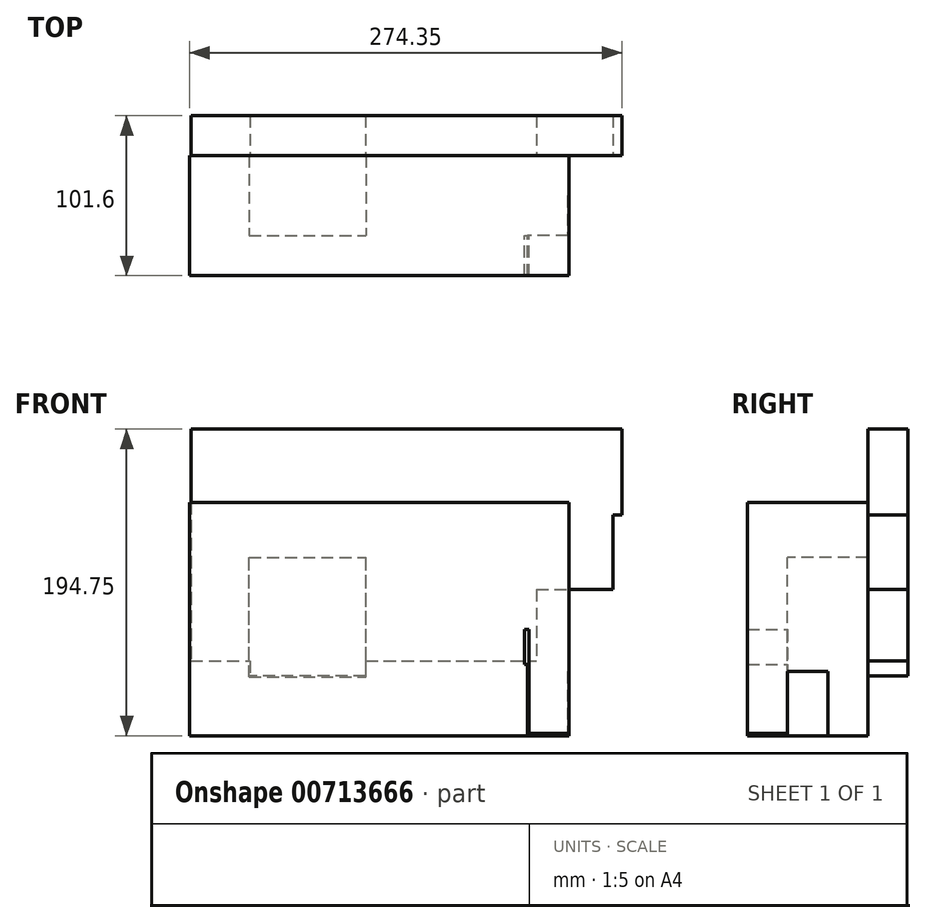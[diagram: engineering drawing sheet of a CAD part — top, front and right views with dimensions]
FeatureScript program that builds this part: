
annotation { "Feature Type Name" : "Feature", "Feature Type Description" : "" }
export const myFeature = defineFeature(function(context is Context, id is Id, definition is map)
    precondition{}
    {
        {
            var Q0;
            Q0=qCreatedBy(makeId("Front.planeOp"),FACE);
            var sketch = newSketch(context, id + "F0", { "sketchPlane" : qUnion([Q0])});
            skLineSegment(sketch, "E0.bottom", {"start": v(-136.7, -9.97) * mm, "end": v(75.91, -9.97) * mm});
            skLineSegment(sketch, "E0.top", {"start": v(-136.7, -32.2) * mm, "end": v(75.91, -32.2) * mm});
            skLineSegment(sketch, "E0.left", {"start": v(-136.7, -9.97) * mm, "end": v(-136.7, -32.2) * mm});
            skLineSegment(sketch, "E0.right", {"start": v(75.91, -9.97) * mm, "end": v(75.91, -32.2) * mm});
            skLineSegment(sketch, "E1.bottom", {"start": v(-136.7, -32.2) * mm, "end": v(77.82, -32.2) * mm});
            skLineSegment(sketch, "E1.top", {"start": v(-136.7, -77.37) * mm, "end": v(77.82, -77.37) * mm});
            skLineSegment(sketch, "E1.left", {"start": v(-136.7, -32.2) * mm, "end": v(-136.7, -77.37) * mm});
            skLineSegment(sketch, "E1.right", {"start": v(77.82, -32.2) * mm, "end": v(77.82, -77.37) * mm});
            skLineSegment(sketch, "E2.bottom", {"start": v(-136.7, -9.97) * mm, "end": v(78.83, -9.97) * mm});
            skLineSegment(sketch, "E2.top", {"start": v(-136.7, 70.86) * mm, "end": v(78.83, 70.86) * mm});
            skLineSegment(sketch, "E2.left", {"start": v(-136.7, -9.97) * mm, "end": v(-136.7, 70.86) * mm});
            skLineSegment(sketch, "E2.right", {"start": v(78.83, -9.97) * mm, "end": v(78.83, 70.86) * mm});
            skSolve(sketch);
        }
        {
            var Q0;
            Q0 = qSketchRegion(id + "F0", true);
            extrude(context, id + "F1", {"entities" : qUnion([Q0]), "depth" : 25.4 * mm, "offsetDistance" : 25.4 * mm});
        }
        {
            var Q0;
            Q0=makeQuery(id+"F1.opExtrude","SWEPT_FACE",FACE,{"disambiguationData":[OSD([sQuery(id+"F0.wireOp",EDGE,"E2.right")])]});
            var sketch = newSketch(context, id + "F2", { "sketchPlane" : qUnion([Q0])});
            skPoint(sketch, "E3.oppositeSnap0", {"position": v(-25.4, 30.45) * mm});
            skLineSegment(sketch, "E3.bottom", {"start": v(0, 70.86) * mm, "end": v(-25.4, 70.86) * mm});
            skLineSegment(sketch, "E3.top", {"start": v(0, -75.8) * mm, "end": v(-25.4, -75.8) * mm});
            skLineSegment(sketch, "E3.left", {"start": v(0, 70.86) * mm, "end": v(0, -75.8) * mm});
            skLineSegment(sketch, "E3.right", {"start": v(-25.4, 70.86) * mm, "end": v(-25.4, -75.8) * mm});
            skLineSegment(sketch, "E4.bottom", {"start": v(-13.69, 30.45) * mm, "end": v(0, 30.45) * mm});
            skLineSegment(sketch, "E4.top", {"start": v(-13.69, -9.97) * mm, "end": v(0, -9.97) * mm});
            skLineSegment(sketch, "E4.left", {"start": v(-13.69, 30.45) * mm, "end": v(-13.69, -9.97) * mm});
            skLineSegment(sketch, "E4.right", {"start": v(0, 30.45) * mm, "end": v(0, -9.97) * mm});
            skSolve(sketch);
        }
        {
            var Q0;
            Q0 = qSketchRegion(id + "F2", true);
            extrude(context, id + "F3", {"entities" : qUnion([Q0]), "operationType" : NewBodyOperationType.ADD, "depth" : 25.4 * mm, "offsetDistance" : 25.4 * mm});
        }
        {
            var Q0;
            Q0=makeQuery(id+"F3.boolean.opBoolean","MERGE",FACE,{"derivedFrom":[makeQuery(id+"F1.opExtrude","CAP_FACE",FACE,{"disambiguationData":[OSD([sQuery(id+"F0.wireOp",EDGE,"E0.left"),sQuery(id+"F0.wireOp",EDGE,"E0.right"),sQuery(id+"F0.wireOp",EDGE,"E1.bottom"),sQuery(id+"F0.wireOp",EDGE,"E1.top"),sQuery(id+"F0.wireOp",EDGE,"E1.left"),sQuery(id+"F0.wireOp",EDGE,"E1.right"),sQuery(id+"F0.wireOp",EDGE,"E2.bottom"),sQuery(id+"F0.wireOp",EDGE,"E2.top"),sQuery(id+"F0.wireOp",EDGE,"E2.left"),sQuery(id+"F0.wireOp",EDGE,"E2.right")])],"isStart":true}),makeQuery(id+"F3.opExtrude","SWEPT_FACE",FACE,{"disambiguationData":[OSD([sQuery(id+"F2.wireOp",EDGE,"E3.left"),sQuery(id+"F2.wireOp",EDGE,"E4.right")])]})]});
            var sketch = newSketch(context, id + "F4", { "sketchPlane" : qUnion([Q0])});
            skLineSegment(sketch, "E5.bottom", {"start": v(75.8, -77.37) * mm, "end": v(136.7, -77.37) * mm});
            skLineSegment(sketch, "E5.top", {"start": v(75.8, 70.86) * mm, "end": v(136.7, 70.86) * mm});
            skLineSegment(sketch, "E5.left", {"start": v(75.8, -77.37) * mm, "end": v(75.8, 70.86) * mm});
            skLineSegment(sketch, "E5.right", {"start": v(136.7, -77.37) * mm, "end": v(136.7, 70.86) * mm});
            skLineSegment(sketch, "E6.bottom", {"start": v(75.8, 70.86) * mm, "end": v(-17.93, 70.86) * mm});
            skLineSegment(sketch, "E6.top", {"start": v(75.8, -77.37) * mm, "end": v(-17.93, -77.37) * mm});
            skLineSegment(sketch, "E6.left", {"start": v(75.8, 70.86) * mm, "end": v(75.8, -77.37) * mm});
            skLineSegment(sketch, "E6.right", {"start": v(-17.93, 70.86) * mm, "end": v(-17.93, -77.37) * mm});
            skLineSegment(sketch, "E7.bottom", {"start": v(-17.93, -77.37) * mm, "end": v(-17.93, -77.37) * mm});
            skLineSegment(sketch, "E7.top", {"start": v(-17.93, 70.86) * mm, "end": v(-17.93, 70.86) * mm});
            skLineSegment(sketch, "E7.left", {"start": v(-17.93, -77.37) * mm, "end": v(-17.93, 70.86) * mm});
            skLineSegment(sketch, "E7.right", {"start": v(-17.93, -77.37) * mm, "end": v(-17.93, 70.86) * mm});
            skLineSegment(sketch, "E8.bottom", {"start": v(99.08, -40.05) * mm, "end": v(24.74, -40.05) * mm});
            skLineSegment(sketch, "E8.top", {"start": v(99.08, 35.82) * mm, "end": v(24.74, 35.82) * mm});
            skLineSegment(sketch, "E8.left", {"start": v(99.08, -40.05) * mm, "end": v(99.08, 35.82) * mm});
            skLineSegment(sketch, "E8.right", {"start": v(24.74, -40.05) * mm, "end": v(24.74, 35.82) * mm});
            skSolve(sketch);
        }
        {
            var Q0;
            Q0 = qSketchRegion(id + "F4", true);
            extrude(context, id + "F5", {"entities" : qUnion([Q0]), "operationType" : NewBodyOperationType.ADD, "depth" : 25.4 * mm, "offsetDistance" : 25.4 * mm});
        }
        {
            var Q0;
            Q0=makeQuery(id+"F5.opExtrude","CAP_FACE",FACE,{"disambiguationData":[OSD([sQuery(id+"F4.wireOp",EDGE,"E5.bottom"),sQuery(id+"F4.wireOp",EDGE,"E5.top"),sQuery(id+"F4.wireOp",EDGE,"E5.right"),sQuery(id+"F4.wireOp",EDGE,"E6.bottom"),sQuery(id+"F4.wireOp",EDGE,"E6.top"),sQuery(id+"F4.wireOp",EDGE,"E7.right"),sQuery(id+"F4.wireOp",EDGE,"E8.bottom"),sQuery(id+"F4.wireOp",EDGE,"E8.top"),sQuery(id+"F4.wireOp",EDGE,"E8.left"),sQuery(id+"F4.wireOp",EDGE,"E8.right")])],"isStart":false});
            var sketch = newSketch(context, id + "F6", { "sketchPlane" : qUnion([Q0])});
            skLineSegment(sketch, "E9.bottom", {"start": v(77.95, 14.77) * mm, "end": v(-17.93, 14.77) * mm});
            skLineSegment(sketch, "E9.top", {"start": v(77.95, 70.86) * mm, "end": v(-17.93, 70.86) * mm});
            skLineSegment(sketch, "E9.left", {"start": v(77.95, 14.77) * mm, "end": v(77.95, 70.86) * mm});
            skLineSegment(sketch, "E9.right", {"start": v(-17.93, 14.77) * mm, "end": v(-17.93, 70.86) * mm});
            skLineSegment(sketch, "E10.bottom", {"start": v(77.95, 70.86) * mm, "end": v(136.7, 70.86) * mm});
            skLineSegment(sketch, "E10.top", {"start": v(77.95, -77.37) * mm, "end": v(136.7, -77.37) * mm});
            skLineSegment(sketch, "E10.left", {"start": v(77.95, 70.86) * mm, "end": v(77.95, -77.37) * mm});
            skLineSegment(sketch, "E10.right", {"start": v(136.7, 70.86) * mm, "end": v(136.7, -77.37) * mm});
            skLineSegment(sketch, "E11.bottom", {"start": v(77.95, -77.37) * mm, "end": v(-17.93, -77.37) * mm});
            skLineSegment(sketch, "E11.left", {"start": v(77.95, -77.37) * mm, "end": v(77.95, 14.77) * mm});
            skLineSegment(sketch, "E11.right", {"start": v(-17.93, -77.37) * mm, "end": v(-17.93, 14.77) * mm});
            skLineSegment(sketch, "E12.bottom", {"start": v(24.74, 35.82) * mm, "end": v(99.08, 35.82) * mm});
            skLineSegment(sketch, "E12.top", {"start": v(24.74, -40.05) * mm, "end": v(99.08, -40.05) * mm});
            skLineSegment(sketch, "E12.left", {"start": v(24.74, 35.82) * mm, "end": v(24.74, -40.05) * mm});
            skLineSegment(sketch, "E12.right", {"start": v(99.08, 35.82) * mm, "end": v(99.08, -40.05) * mm});
            skSolve(sketch);
        }
        {
            var Q0;
            Q0 = qSketchRegion(id + "F6", true);
            extrude(context, id + "F7", {"entities" : qUnion([Q0]), "operationType" : NewBodyOperationType.ADD, "depth" : 25.4 * mm, "offsetDistance" : 25.4 * mm});
        }
        {
            var Q0;
            {var subQ0=sQuery(id+"F2.wireOp",EDGE,"E4.right");var subQ2=sQuery(id+"F2.wireOp",EDGE,"E3.left");var subQ5=sQuery(id+"F0.wireOp",EDGE,"E1.top");var subQ6=sQuery(id+"F0.wireOp",EDGE,"E1.bottom");var subQ7=sQuery(id+"F0.wireOp",EDGE,"E2.top");var subQ8=sQuery(id+"F0.wireOp",EDGE,"E2.bottom");var subQ9=sQuery(id+"F0.wireOp",EDGE,"E1.right");var subQ10=sQuery(id+"F0.wireOp",EDGE,"E0.right");Q0=makeQuery(id+"F5.boolean.opBoolean","SPLIT",FACE,{"disambiguationData":[TD([makeQuery(id+"F1.opExtrude","SWEPT_FACE",FACE,{"disambiguationData":[OSD([subQ10])]})])],"derivedFrom":makeQuery(id+"F3.boolean.opBoolean","MERGE",FACE,{"derivedFrom":[makeQuery(id+"F1.opExtrude","CAP_FACE",FACE,{"disambiguationData":[OSD([sQuery(id+"F0.wireOp",EDGE,"E0.left"),subQ10,subQ6,subQ5,sQuery(id+"F0.wireOp",EDGE,"E1.left"),subQ9,subQ8,subQ7,sQuery(id+"F0.wireOp",EDGE,"E2.left"),sQuery(id+"F0.wireOp",EDGE,"E2.right")])],"isStart":true}),makeQuery(id+"F3.opExtrude","SWEPT_FACE",FACE,{"disambiguationData":[OSD([subQ2,subQ0])]})]})});}
            var sketch = newSketch(context, id + "F8", { "sketchPlane" : qUnion([Q0])});
            skLineSegment(sketch, "E13.bottom", {"start": v(-104.23, 70.86) * mm, "end": v(-17.93, 70.86) * mm});
            skLineSegment(sketch, "E13.top", {"start": v(-104.23, -36.6) * mm, "end": v(-17.93, -36.6) * mm});
            skLineSegment(sketch, "E13.left", {"start": v(-104.23, 70.86) * mm, "end": v(-104.23, -36.6) * mm});
            skLineSegment(sketch, "E13.right", {"start": v(-17.93, 70.86) * mm, "end": v(-17.93, -36.6) * mm});
            skSolve(sketch);
        }
        {
            var Q0;
            Q0 = qSketchRegion(id + "F8", true);
            extrude(context, id + "F9", {"entities" : qUnion([Q0]), "operationType" : NewBodyOperationType.ADD, "depth" : 25.4 * mm, "offsetDistance" : 25.4 * mm});
        }
        {
            var Q0;
            {var subQ3=sQuery(id+"F0.wireOp",EDGE,"E1.right");var subQ5=sQuery(id+"F0.wireOp",EDGE,"E1.top");var subQ6=makeQuery(id+"F1.opExtrude","SWEPT_FACE",FACE,{"disambiguationData":[OSD([subQ5])]});var subQ7=sQuery(id+"F2.wireOp",EDGE,"E4.right");var subQ9=sQuery(id+"F2.wireOp",EDGE,"E3.left");var subQ12=sQuery(id+"F0.wireOp",EDGE,"E1.bottom");var subQ13=sQuery(id+"F0.wireOp",EDGE,"E2.top");var subQ14=sQuery(id+"F0.wireOp",EDGE,"E2.bottom");var subQ15=sQuery(id+"F0.wireOp",EDGE,"E0.right");Q0=makeQuery(id+"F9.boolean.opBoolean","SPLIT",FACE,{"disambiguationData":[TD([subQ6])],"derivedFrom":makeQuery(id+"F5.boolean.opBoolean","SPLIT",FACE,{"disambiguationData":[TD([makeQuery(id+"F1.opExtrude","SWEPT_FACE",FACE,{"disambiguationData":[OSD([subQ15])]})])],"derivedFrom":makeQuery(id+"F3.boolean.opBoolean","MERGE",FACE,{"derivedFrom":[makeQuery(id+"F1.opExtrude","CAP_FACE",FACE,{"disambiguationData":[OSD([sQuery(id+"F0.wireOp",EDGE,"E0.left"),subQ15,subQ12,subQ5,sQuery(id+"F0.wireOp",EDGE,"E1.left"),subQ3,subQ14,subQ13,sQuery(id+"F0.wireOp",EDGE,"E2.left"),sQuery(id+"F0.wireOp",EDGE,"E2.right")])],"isStart":true}),makeQuery(id+"F3.opExtrude","SWEPT_FACE",FACE,{"disambiguationData":[OSD([subQ9,subQ7])]})]})})});}
            var sketch = newSketch(context, id + "F10", { "sketchPlane" : qUnion([Q0])});
            skLineSegment(sketch, "E14.bottom", {"start": v(-103.22, -36.6) * mm, "end": v(-17.93, -36.6) * mm});
            skLineSegment(sketch, "E14.top", {"start": v(-103.22, -77.37) * mm, "end": v(-17.93, -77.37) * mm});
            skLineSegment(sketch, "E14.left", {"start": v(-103.22, -36.6) * mm, "end": v(-103.22, -77.37) * mm});
            skLineSegment(sketch, "E14.right", {"start": v(-17.93, -36.6) * mm, "end": v(-17.93, -77.37) * mm});
            skSolve(sketch);
        }
        {
            var Q0;
            Q0 = qSketchRegion(id + "F10", true);
            extrude(context, id + "F11", {"entities" : qUnion([Q0]), "operationType" : NewBodyOperationType.ADD, "depth" : 25.4 * mm, "offsetDistance" : 25.4 * mm});
        }
        {
            var Q0;
            Q0=makeQuery(id+"F11.boolean.opBoolean","MERGE",FACE,{"derivedFrom":[makeQuery(id+"F9.opExtrude","CAP_FACE",FACE,{"disambiguationData":[OSD([sQuery(id+"F8.wireOp",EDGE,"E13.bottom"),sQuery(id+"F8.wireOp",EDGE,"E13.top"),sQuery(id+"F8.wireOp",EDGE,"E13.left"),sQuery(id+"F8.wireOp",EDGE,"E13.right")])],"isStart":false}),makeQuery(id+"F11.opExtrude","CAP_FACE",FACE,{"disambiguationData":[OSD([sQuery(id+"F10.wireOp",EDGE,"E14.bottom"),sQuery(id+"F10.wireOp",EDGE,"E14.top"),sQuery(id+"F10.wireOp",EDGE,"E14.left"),sQuery(id+"F10.wireOp",EDGE,"E14.right")])],"isStart":false})]});
            var sketch = newSketch(context, id + "F12", { "sketchPlane" : qUnion([Q0])});
            skLineSegment(sketch, "E15.bottom", {"start": v(-104.23, 70.86) * mm, "end": v(-17.93, 70.86) * mm});
            skLineSegment(sketch, "E15.top", {"start": v(-104.23, -77.37) * mm, "end": v(-17.93, -77.37) * mm});
            skLineSegment(sketch, "E15.left", {"start": v(-104.23, 70.86) * mm, "end": v(-104.23, -77.37) * mm});
            skLineSegment(sketch, "E15.right", {"start": v(-17.93, 70.86) * mm, "end": v(-17.93, -77.37) * mm});
            skSolve(sketch);
        }
        {
            var Q0;
            Q0 = qSketchRegion(id + "F12", true);
            extrude(context, id + "F13", {"entities" : qUnion([Q0]), "operationType" : NewBodyOperationType.ADD, "depth" : 25.4 * mm, "offsetDistance" : 25.4 * mm});
        }
        {
            var Q0;
            Q0=makeQuery(id+"F13.boolean.opBoolean","MERGE",FACE,{"derivedFrom":[makeQuery(id+"F7.opExtrude","CAP_FACE",FACE,{"disambiguationData":[OSD([sQuery(id+"F6.wireOp",EDGE,"E9.top"),sQuery(id+"F6.wireOp",EDGE,"E9.right"),sQuery(id+"F6.wireOp",EDGE,"E10.bottom"),sQuery(id+"F6.wireOp",EDGE,"E10.top"),sQuery(id+"F6.wireOp",EDGE,"E10.right"),sQuery(id+"F6.wireOp",EDGE,"E11.bottom"),sQuery(id+"F6.wireOp",EDGE,"E11.right"),sQuery(id+"F6.wireOp",EDGE,"E12.bottom"),sQuery(id+"F6.wireOp",EDGE,"E12.top"),sQuery(id+"F6.wireOp",EDGE,"E12.left"),sQuery(id+"F6.wireOp",EDGE,"E12.right")])],"isStart":false}),makeQuery(id+"F13.opExtrude","CAP_FACE",FACE,{"disambiguationData":[OSD([sQuery(id+"F12.wireOp",EDGE,"E15.bottom"),sQuery(id+"F12.wireOp",EDGE,"E15.top"),sQuery(id+"F12.wireOp",EDGE,"E15.left"),sQuery(id+"F12.wireOp",EDGE,"E15.right")])],"isStart":false})]});
            var sketch = newSketch(context, id + "F14", { "sketchPlane" : qUnion([Q0])});
            skLineSegment(sketch, "E16.bottom", {"start": v(-104.23, 70.86) * mm, "end": v(70.52, 70.86) * mm});
            skLineSegment(sketch, "E16.top", {"start": v(-104.23, -77.37) * mm, "end": v(70.52, -77.37) * mm});
            skLineSegment(sketch, "E16.left", {"start": v(-104.23, 70.86) * mm, "end": v(-104.23, -77.37) * mm});
            skLineSegment(sketch, "E16.right", {"start": v(70.52, 70.86) * mm, "end": v(70.52, -77.37) * mm});
            skLineSegment(sketch, "E17.bottom", {"start": v(24.74, 35.82) * mm, "end": v(89.08, 35.82) * mm});
            skLineSegment(sketch, "E17.top", {"start": v(24.74, -26.86) * mm, "end": v(89.08, -26.86) * mm});
            skLineSegment(sketch, "E17.left", {"start": v(24.74, 35.82) * mm, "end": v(24.74, -26.86) * mm});
            skLineSegment(sketch, "E17.right", {"start": v(89.08, 35.82) * mm, "end": v(89.08, -26.86) * mm});
            skSolve(sketch);
        }
        {
            var Q0;
            {var subQ1=sQuery(id+"F14.wireOp",EDGE,"E16.bottom");Q0=makeQuery(id+"F14.imprint","IMPRINT",FACE,{"disambiguationData":[TD([[makeQuery(id+"F14.imprint","IMPRINT",EDGE,{"derivedFrom":subQ1}),1.0]])]});}
            var sketch = newSketch(context, id + "F15", { "sketchPlane" : qUnion([Q0])});
            skLineSegment(sketch, "E18.bottom", {"start": v(25.08, 34.42) * mm, "end": v(98.34, 34.42) * mm});
            skLineSegment(sketch, "E18.top", {"start": v(25.08, -39.32) * mm, "end": v(98.34, -39.32) * mm});
            skLineSegment(sketch, "E18.left", {"start": v(25.08, 34.42) * mm, "end": v(25.08, -39.32) * mm});
            skLineSegment(sketch, "E18.right", {"start": v(98.34, 34.42) * mm, "end": v(98.34, -39.32) * mm});
            skLineSegment(sketch, "E19.bottom", {"start": v(135.92, 117.38) * mm, "end": v(-83.47, 117.38) * mm});
            skLineSegment(sketch, "E19.top", {"start": v(135.92, -29.88) * mm, "end": v(-83.47, -29.88) * mm});
            skLineSegment(sketch, "E19.left", {"start": v(135.92, 117.38) * mm, "end": v(135.92, -29.88) * mm});
            skLineSegment(sketch, "E19.right", {"start": v(-83.47, 117.38) * mm, "end": v(-83.47, -29.88) * mm});
            skLineSegment(sketch, "E20.bottom", {"start": v(-83.47, 62.9) * mm, "end": v(-132.05, 62.9) * mm});
            skLineSegment(sketch, "E20.top", {"start": v(-83.47, 15.43) * mm, "end": v(-132.05, 15.43) * mm});
            skLineSegment(sketch, "E20.left", {"start": v(-83.47, 62.9) * mm, "end": v(-83.47, 15.43) * mm});
            skLineSegment(sketch, "E20.right", {"start": v(-132.05, 62.9) * mm, "end": v(-132.05, 15.43) * mm});
            skLineSegment(sketch, "E21.left", {"start": v(-83.47, 62.9) * mm, "end": v(-83.47, 62.9) * mm});
            skLineSegment(sketch, "E21.right", {"start": v(-132.05, 62.9) * mm, "end": v(-132.05, 62.9) * mm});
            skLineSegment(sketch, "E22.bottom", {"start": v(-83.47, 62.9) * mm, "end": v(-137.64, 62.9) * mm});
            skLineSegment(sketch, "E22.top", {"start": v(-83.47, 73.83) * mm, "end": v(-137.64, 73.83) * mm});
            skLineSegment(sketch, "E22.left", {"start": v(-83.47, 62.9) * mm, "end": v(-83.47, 73.83) * mm});
            skLineSegment(sketch, "E22.right", {"start": v(-137.64, 62.9) * mm, "end": v(-137.64, 73.83) * mm});
            skLineSegment(sketch, "E23.bottom", {"start": v(-137.64, 73.83) * mm, "end": v(-83.47, 73.83) * mm});
            skLineSegment(sketch, "E23.top", {"start": v(-137.64, 117.38) * mm, "end": v(-83.47, 117.38) * mm});
            skLineSegment(sketch, "E23.left", {"start": v(-137.64, 73.83) * mm, "end": v(-137.64, 117.38) * mm});
            skLineSegment(sketch, "E23.right", {"start": v(-83.47, 73.83) * mm, "end": v(-83.47, 117.38) * mm});
            skSolve(sketch);
        }
        {
            var Q0;
            Q0 = qSketchRegion(id + "F15", true);
            extrude(context, id + "F16", {"entities" : qUnion([Q0]), "operationType" : NewBodyOperationType.ADD, "depth" : 25.4 * mm, "offsetDistance" : 25.4 * mm});
        }
    });
